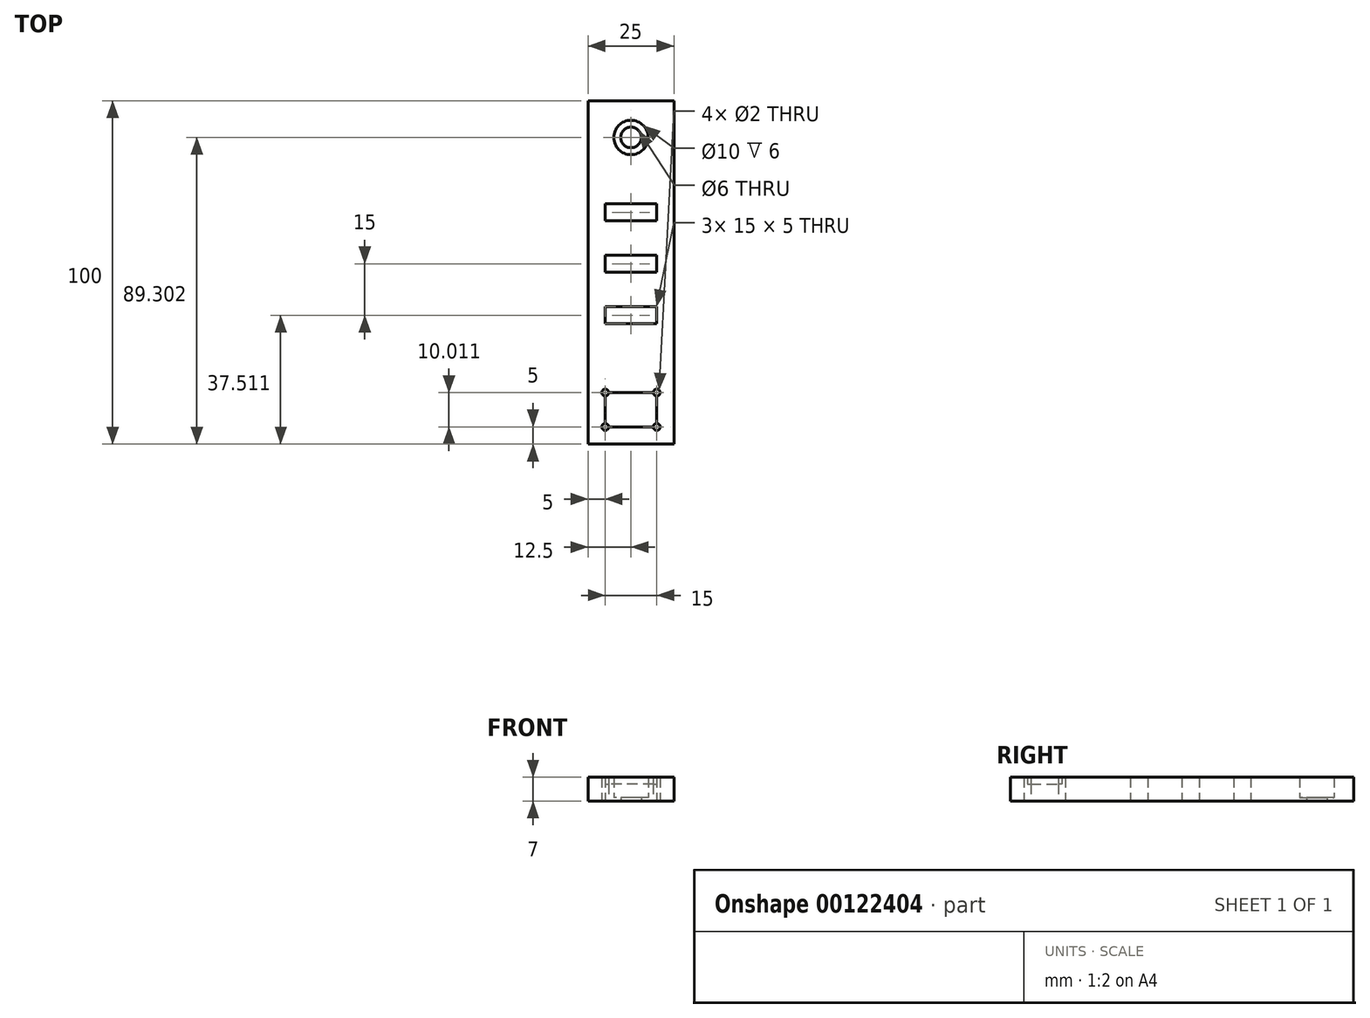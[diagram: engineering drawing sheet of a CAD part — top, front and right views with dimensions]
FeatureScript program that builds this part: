
annotation { "Feature Type Name" : "Feature", "Feature Type Description" : "" }
export const myFeature = defineFeature(function(context is Context, id is Id, definition is map)
    precondition{}
    {
        {
            var Q0;
            Q0=qCreatedBy(makeId("Top.planeOp"),FACE);
            var sketch = newSketch(context, id + "F0", { "sketchPlane" : qUnion([Q0])});
            skLineSegment(sketch, "E0.bottom", {"start": v(12.5, -50) * mm, "end": v(-12.5, -50) * mm});
            skLineSegment(sketch, "E0.top", {"start": v(12.5, 50) * mm, "end": v(-12.5, 50) * mm});
            skLineSegment(sketch, "E0.left", {"start": v(12.5, -50) * mm, "end": v(12.5, 50) * mm});
            skLineSegment(sketch, "E0.right", {"start": v(-12.5, -50) * mm, "end": v(-12.5, 50) * mm});
            skPoint(sketch, "E0.middle", {"position": v(0, 0) * mm});
            skLineSegment(sketch, "E1", {"start": v(0, 50) * mm, "end": v(0, -50) * mm});
            skCircle(sketch, "E2", {"center": v(0, 39.3) * mm, "radius": 2.5 * mm});
            skCircle(sketch, "E3", {"center": v(0, 39.3) * mm, "radius": 3 * mm});
            skCircle(sketch, "E4", {"center": v(0, 39.3) * mm, "radius": 5 * mm});
            skLineSegment(sketch, "E5.bottom", {"start": v(-7.5, -34.99) * mm, "end": v(7.5, -34.99) * mm});
            skLineSegment(sketch, "E5.top", {"start": v(-7.5, -45) * mm, "end": v(7.5, -45) * mm});
            skLineSegment(sketch, "E5.left", {"start": v(-7.5, -34.99) * mm, "end": v(-7.5, -45) * mm});
            skLineSegment(sketch, "E5.right", {"start": v(7.5, -34.99) * mm, "end": v(7.5, -45) * mm});
            skCircle(sketch, "E6", {"center": v(-7.5, -34.99) * mm, "radius": 1 * mm});
            skCircle(sketch, "E7", {"center": v(7.5, -34.99) * mm, "radius": 1 * mm});
            skCircle(sketch, "E8", {"center": v(-7.5, -45) * mm, "radius": 1 * mm});
            skCircle(sketch, "E9", {"center": v(7.5, -45) * mm, "radius": 1 * mm});
            skLineSegment(sketch, "E10.bottom", {"start": v(-7.5, 20.01) * mm, "end": v(7.5, 20.01) * mm});
            skLineSegment(sketch, "E10.top", {"start": v(-7.5, 15.01) * mm, "end": v(7.5, 15.01) * mm});
            skLineSegment(sketch, "E10.left", {"start": v(-7.5, 20.01) * mm, "end": v(-7.5, 15.01) * mm});
            skLineSegment(sketch, "E10.right", {"start": v(7.5, 20.01) * mm, "end": v(7.5, 15.01) * mm});
            skLineSegment(sketch, "E11.bottom", {"start": v(-7.5, 5.01) * mm, "end": v(7.5, 5.01) * mm});
            skLineSegment(sketch, "E11.top", {"start": v(-7.5, 0.01) * mm, "end": v(7.5, 0.01) * mm});
            skLineSegment(sketch, "E11.left", {"start": v(-7.5, 5.01) * mm, "end": v(-7.5, 0.01) * mm});
            skLineSegment(sketch, "E11.right", {"start": v(7.5, 5.01) * mm, "end": v(7.5, 0.01) * mm});
            skLineSegment(sketch, "E12.bottom", {"start": v(-7.5, -9.99) * mm, "end": v(7.5, -9.99) * mm});
            skLineSegment(sketch, "E12.top", {"start": v(-7.5, -14.99) * mm, "end": v(7.5, -14.99) * mm});
            skLineSegment(sketch, "E12.left", {"start": v(-7.5, -9.99) * mm, "end": v(-7.5, -14.99) * mm});
            skLineSegment(sketch, "E12.right", {"start": v(7.5, -9.99) * mm, "end": v(7.5, -14.99) * mm});
            skSolve(sketch);
        }
        {
            var Q0;
            {var subQ12=sQuery(id+"F0.wireOp",EDGE,"E0.right");Q0=makeQuery(id+"F0.imprint","IMPRINT",FACE,{"disambiguationData":[TD([[makeQuery(id+"F0.imprint","IMPRINT",EDGE,{"derivedFrom":subQ12}),-1.0]])]});}
            var Q1;
            {var subQ12=sQuery(id+"F0.wireOp",EDGE,"E0.left");Q1=makeQuery(id+"F0.imprint","IMPRINT",FACE,{"disambiguationData":[TD([[makeQuery(id+"F0.imprint","IMPRINT",EDGE,{"derivedFrom":subQ12}),1.0]])]});}
            var Q2;
            {var subQ5=sQuery(id+"F0.wireOp",EDGE,"E5.bottom");var subQ6=sQuery(id+"F0.wireOp",EDGE,"E1");var subQ7=makeQuery(id+"F0.imprint","INTERSECT",VERTEX,{"derivedFrom":[subQ6,subQ5]});Q2=makeQuery(id+"F0.imprint","IMPRINT",FACE,{"disambiguationData":[TD([[makeQuery(id+"F0.imprint","IMPRINT",EDGE,{"disambiguationData":[TD([[subQ7,-1.0]])],"derivedFrom":subQ6}),1.0]])]});}
            var Q3;
            {var subQ1=sQuery(id+"F0.wireOp",EDGE,"E1");var subQ5=sQuery(id+"F0.wireOp",EDGE,"E5.bottom");var subQ6=makeQuery(id+"F0.imprint","INTERSECT",VERTEX,{"derivedFrom":[subQ1,subQ5]});Q3=makeQuery(id+"F0.imprint","IMPRINT",FACE,{"disambiguationData":[TD([[makeQuery(id+"F0.imprint","IMPRINT",EDGE,{"disambiguationData":[TD([[subQ6,-1.0]])],"derivedFrom":subQ1}),-1.0]])]});}
            extrude(context, id + "F1", {"entities" : qUnion([Q0, Q1, Q2, Q3]), "depth" : 5 * mm});
        }
        {
            var Q0;
            {var subQ0=sQuery(id+"F0.wireOp",EDGE,"E4");var subQ1=sQuery(id+"F0.wireOp",EDGE,"E1");var subQ2=makeQuery(id+"F0.imprint","INTERSECT",VERTEX,{"disambiguationData":[OD(0.0)],"derivedFrom":[subQ1,subQ0]});Q0=makeQuery(id+"F0.imprint","IMPRINT",FACE,{"disambiguationData":[TD([[makeQuery(id+"F0.imprint","IMPRINT",EDGE,{"disambiguationData":[TD([[subQ2,-1.0]])],"derivedFrom":subQ1}),-1.0]])]});}
            var Q1;
            {var subQ0=sQuery(id+"F0.wireOp",EDGE,"E4");var subQ1=sQuery(id+"F0.wireOp",EDGE,"E1");var subQ2=makeQuery(id+"F0.imprint","INTERSECT",VERTEX,{"disambiguationData":[OD(0.0)],"derivedFrom":[subQ1,subQ0]});Q1=makeQuery(id+"F0.imprint","IMPRINT",FACE,{"disambiguationData":[TD([[makeQuery(id+"F0.imprint","IMPRINT",EDGE,{"disambiguationData":[TD([[subQ2,-1.0]])],"derivedFrom":subQ1}),1.0]])]});}
            extrude(context, id + "F2", {"entities" : qUnion([Q0, Q1]), "operationType" : NewBodyOperationType.ADD, "depth" : 7 * mm});
        }
        {
            var Q0;
            {var subQ0=sQuery(id+"F0.wireOp",EDGE,"E3");var subQ1=sQuery(id+"F0.wireOp",EDGE,"E1");var subQ2=makeQuery(id+"F0.imprint","INTERSECT",VERTEX,{"disambiguationData":[OD(0.0)],"derivedFrom":[subQ1,subQ0]});Q0=makeQuery(id+"F0.imprint","IMPRINT",FACE,{"disambiguationData":[TD([[makeQuery(id+"F0.imprint","IMPRINT",EDGE,{"disambiguationData":[TD([[subQ2,-1.0]])],"derivedFrom":subQ1}),-1.0]])]});}
            var Q1;
            {var subQ0=sQuery(id+"F0.wireOp",EDGE,"E3");var subQ1=sQuery(id+"F0.wireOp",EDGE,"E1");var subQ2=makeQuery(id+"F0.imprint","INTERSECT",VERTEX,{"disambiguationData":[OD(0.0)],"derivedFrom":[subQ1,subQ0]});Q1=makeQuery(id+"F0.imprint","IMPRINT",FACE,{"disambiguationData":[TD([[makeQuery(id+"F0.imprint","IMPRINT",EDGE,{"disambiguationData":[TD([[subQ2,-1.0]])],"derivedFrom":subQ1}),1.0]])]});}
            extrude(context, id + "F3", {"entities" : qUnion([Q0, Q1]), "operationType" : NewBodyOperationType.ADD, "depth" : 1 * mm});
        }
    });
